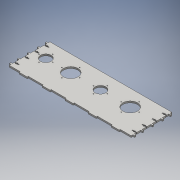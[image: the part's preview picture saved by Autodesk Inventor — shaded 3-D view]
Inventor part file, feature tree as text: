
AUTODESK INVENTOR PART (.ipt)
format: ipt  version: 2016 (Build 200138000, 138)  size: 520,192 bytes
history: native  units: mm
features: sketch x4, extrude x3, projected_geometry x3, other x1
ambient origin geometry x8: Origin, YZ Plane, XZ Plane, XY Plane, X Axis, Y Axis, Z Axis, Center Point
bodies: Body1 (feature_tree)
feature tree (11):
  other  "Sólido1"
  extrude  "Extrusión1"  Depth=150.0mm
  extrude  "Extrusión2"  Depth=60.0mm
  extrude  "Extrusión3"  Depth=45.0mm
  sketch  "Boceto6"  dims[d11=91.8mm d12=39.0mm d14=90.0mm d15=39.0mm d16=90.0mm d17=14.266667mm d19=54.0mm d20=109.8mm d21=109.8mm d22=6.0mm d23=0.0mm d25=3.0mm d26=33.0mm d27=40.0mm d29=360.0deg d31=3.0mm d32=33.0mm d33=40.0mm d35=360.0deg d37=6.0mm d38=0.0mm d44=3.0mm d45=25.5mm d46=40.0mm d48=360.0deg d50=3.0mm d51=25.5mm d52=40.0mm d54=360.0deg d56=6.0mm d57=0.0mm d58=6.2mm d59=6.2mm d60=2.8mm d61=2.8mm d62=450.0mm d63=450.0mm d64=450.0mm d65=450.0mm d67=15.0mm d68=15.0mm d69=6.0mm d70=5.0mm]
  sketch  "Boceto1"  dims[d0=450.0mm d1=150.0mm]
  sketch  "Boceto2"  dims[d6=54.0mm d7=60.0mm]
  projected_geometry  "Contorno proyectado1"
  sketch  "Boceto3"  dims[d9=90.0mm d10=45.0mm]
  projected_geometry  "Contorno proyectado2"
  projected_geometry  "Contorno proyectado5"
